# Revit family: 3-101-xx - Oslo (Ceiling Fan)
name_source: partatom
category: Lighting Fixtures
revit_build: Autodesk Revit 2018 (Build: 20170223_1515(x64)
units: mm (PartAtom-declared; Revit-internal decimal feet)

## family parameters
Always vertical = Yes
Cut with Voids When Loaded = No
Host = Ceiling
Light Source = Yes
OmniClass Number = 23.80.70.11
OmniClass Title = Luminaries for Internal Lighting
Part Type = Normal
Room Calculation Point = No
Round Connector Dimension = Use Diameter
Shared = No

## types (8) — shared parameters
Assembly Code = --
Color Filter = 16777215
Description = --
Dimming Lamp Color Temperature Shift = <None>
Emit Shape Visible in Rendering = No
Emit from Circle Diameter = 7 "
Input Voltage = 120 V 50/60 Hz
Keynote = LED array lamp
Lamp = LED Array
Light Source Symbol Size = 24 "
Manufacturer = Oxygen Lighting
Model = 3-101-xx - Oslo
Type Comments = LED Lighting Fixture
URL = www.oxygenlighting.com
zero-valued in all types: Cost

## per-type parameters (varying)
| type | Diffuser | Metal Finish |
| 3-101-20 - Oslo | Oxygen Lighting - Diffuser - Matte White Acrylic | Oxygen Lighting - Metal Finish - 20 - Polished Nickel |
| 3-101-22 - Oslo | Oxygen Lighting - Diffuser - Matte White Acrylic | Oxygen Lighting - Metal Finish - 22 - Oiled Bronze |
| 3-101-24 - Oslo | Oxygen Lighting - Diffuser - Matte White Acrylic | Oxygen Lighting - Metal Finish - 24 - Satin Nickel |
| 3-101-06 - Oslo | Oxygen Lighting - Diffuser - Matte White Acrylic | Oxygen Lighting - Metal Finish - 06 - White |
| 3-101-06 - Oslo (Without light kit) | Oxygen Lighting - Metal Finish - 06 - White | Oxygen Lighting - Metal Finish - 06 - White |
| 3-101-20 - Oslo (Without light kit) | Oxygen Lighting - Metal Finish - 20 - Polished Nickel | Oxygen Lighting - Metal Finish - 20 - Polished Nickel |
| 3-101-22 - Oslo (Without light kit) | Oxygen Lighting - Metal Finish - 22 - Oiled Bronze | Oxygen Lighting - Metal Finish - 22 - Oiled Bronze |
| 3-101-24 - Oslo (Without light kit) | Oxygen Lighting - Metal Finish - 24 - Satin Nickel | Oxygen Lighting - Metal Finish - 24 - Satin Nickel |

## geometry (parser evidence)
native form markers: Sweep x2
no freeform markers — native parametric forms only
